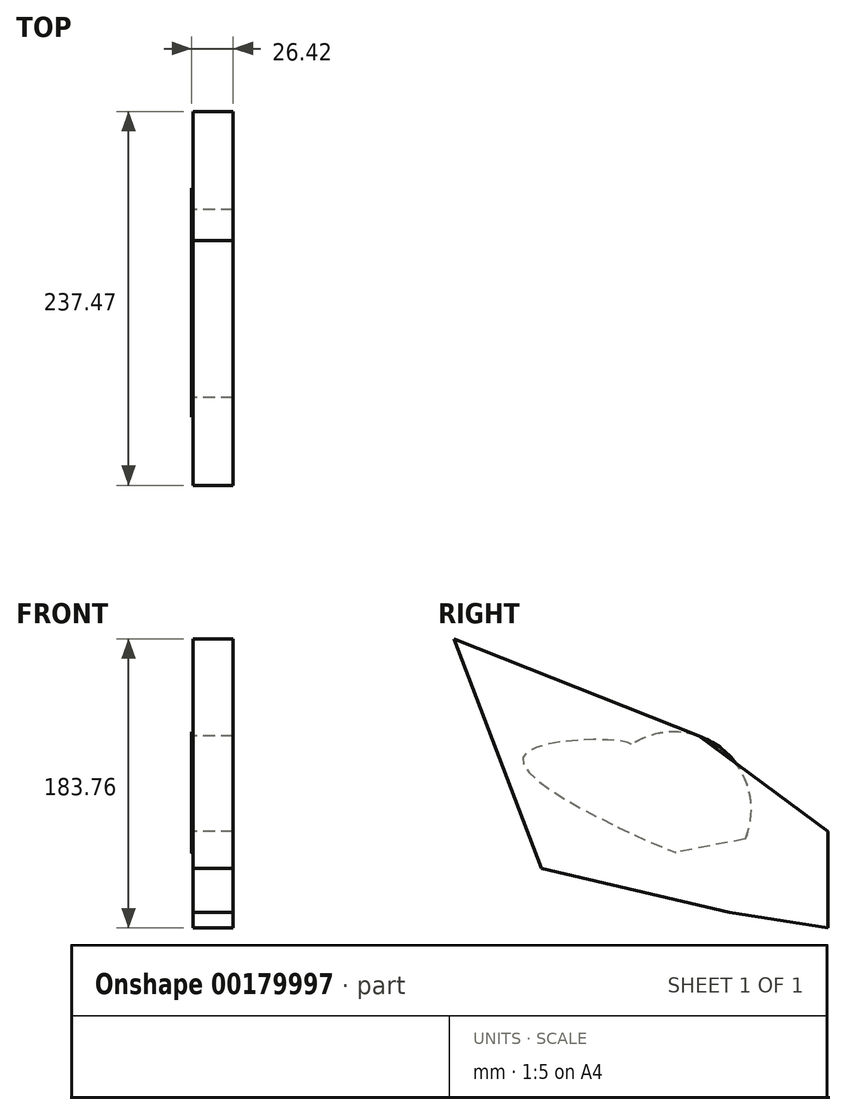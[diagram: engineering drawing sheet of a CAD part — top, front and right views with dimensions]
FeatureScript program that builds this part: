
annotation { "Feature Type Name" : "Feature", "Feature Type Description" : "" }
export const myFeature = defineFeature(function(context is Context, id is Id, definition is map)
    precondition{}
    {
        {
            var Q0;
            Q0=qCreatedBy(makeId("Right.planeOp"),FACE);
            var sketch = newSketch(context, id + "F0", { "sketchPlane" : qUnion([Q0])});
            skArc(sketch, "E0", {"start": v(44.33, 8.59) * mm, "mid": v(30.2, 65.2) * mm, "end": v(-28.04, 68.67) * mm});
            skLineSegment(sketch, "E1", {"start": v(-1.28, 27.28) * mm, "end": v(-28.04, 68.67) * mm});
            skLineSegment(sketch, "E2", {"start": v(0, 0) * mm, "end": v(-1.28, 27.28) * mm});
            skLineSegment(sketch, "E3", {"start": v(44.33, 8.59) * mm, "end": v(-0.64, 0) * mm});
            skPoint(sketch, "E3.endSnap0", {"position": v(-0.64, 13.64) * mm});
            skFitSpline(sketch, "E4", {"points": [v(0, 0) * mm, v(-28.5, 19.54) * mm, v(-18.55, 31.8) * mm, v(-42.52, 56.32) * mm, v(-28.04, 68.67) * mm, v(-97.25, 59.4) * mm, v(0, 0) * mm]});
            skSolve(sketch);
        }
        {
            var Q0;
            Q0 = qSketchRegion(id + "F0", true);
            extrude(context, id + "F1", {"entities" : qUnion([Q0]), "depth" : 1.02 * mm});
        }
        {
            var Q0;
            Q0=makeQuery(id+"F1.opExtrude","CAP_FACE",FACE,{"disambiguationData":[OSD([sQuery(id+"F0.wireOp",EDGE,"E0"),sQuery(id+"F0.wireOp",EDGE,"E2"),sQuery(id+"F0.wireOp",EDGE,"E3"),sQuery(id+"F0.wireOp",EDGE,"E4")])],"isStart":false});
            var sketch = newSketch(context, id + "F2", { "sketchPlane" : qUnion([Q0])});
            skLineSegment(sketch, "E5", {"start": v(0, 0) * mm, "end": v(34.27, -37.97) * mm});
            skLineSegment(sketch, "E6", {"start": v(34.27, -37.97) * mm, "end": v(96.69, -48.03) * mm});
            skLineSegment(sketch, "E7", {"start": v(96.69, -48.03) * mm, "end": v(96.69, 13.4) * mm});
            skLineSegment(sketch, "E8", {"start": v(96.69, 13.4) * mm, "end": v(14.65, 73.92) * mm});
            skLineSegment(sketch, "E9", {"start": v(14.65, 73.92) * mm, "end": v(-140.78, 135.73) * mm});
            skLineSegment(sketch, "E10", {"start": v(-140.78, 135.73) * mm, "end": v(-85.15, -10) * mm});
            skLineSegment(sketch, "E11", {"start": v(-85.15, -10) * mm, "end": v(34.27, -37.97) * mm});
            skSolve(sketch);
        }
        {
            var Q0;
            Q0 = qSketchRegion(id + "F2", true);
            extrude(context, id + "F3", {"entities" : qUnion([Q0]), "operationType" : NewBodyOperationType.ADD, "depth" : 25.4 * mm});
        }
    });
